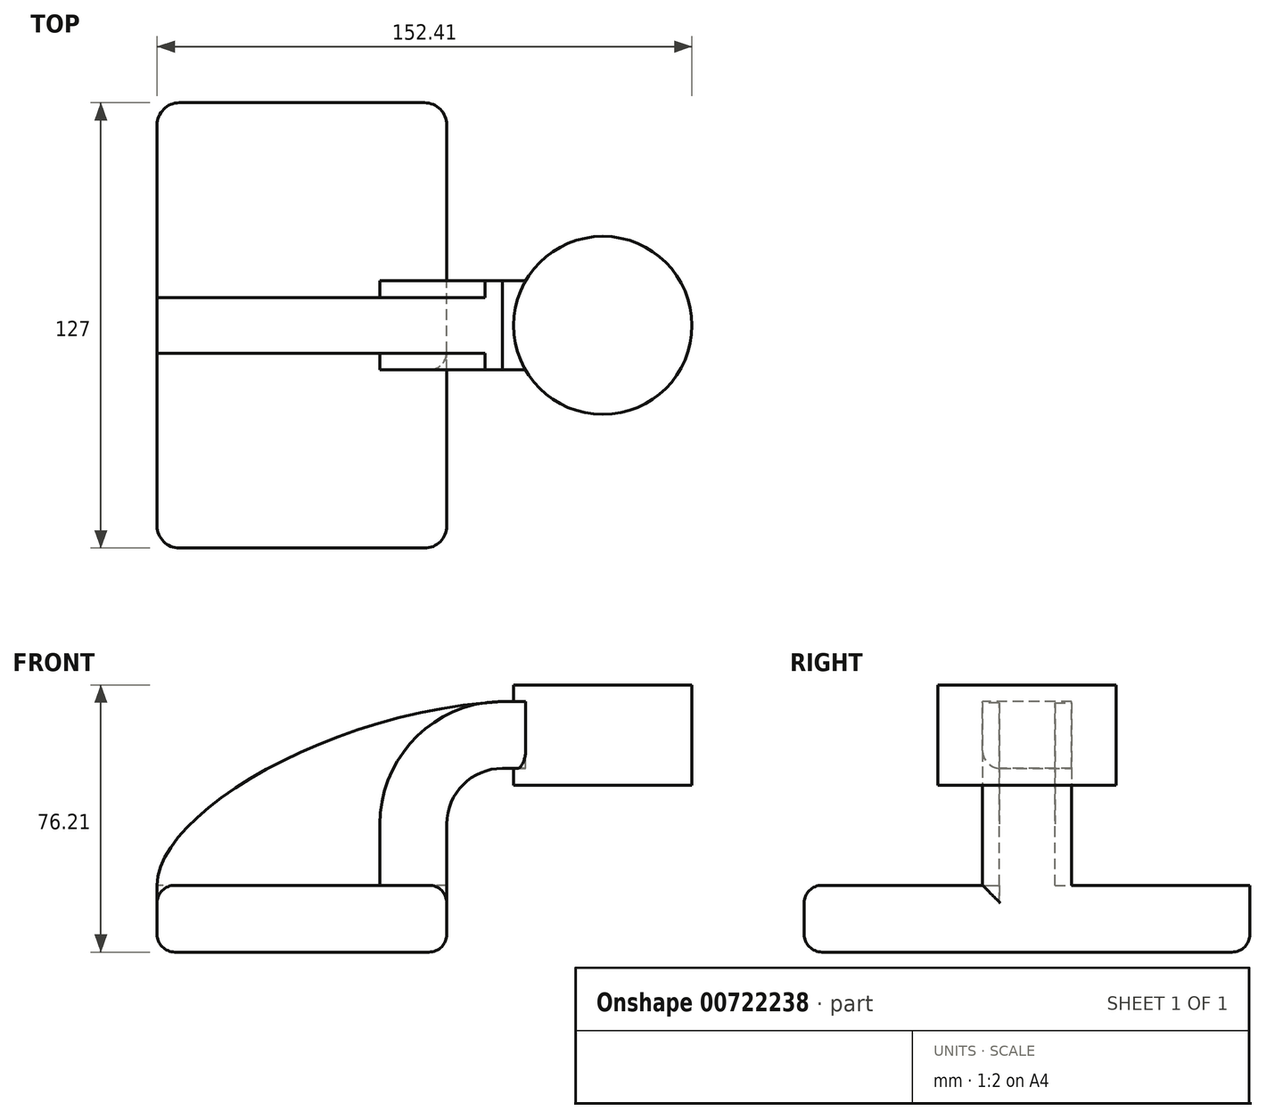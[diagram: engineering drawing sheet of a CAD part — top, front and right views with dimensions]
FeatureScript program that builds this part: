
annotation { "Feature Type Name" : "Feature", "Feature Type Description" : "" }
export const myFeature = defineFeature(function(context is Context, id is Id, definition is map)
    precondition{}
    {
        {
            var Q0;
            Q0=qCreatedBy(makeId("Front.planeOp"),FACE);
            var sketch = newSketch(context, id + "F0", { "sketchPlane" : qUnion([Q0])});
            skLineSegment(sketch, "E0.bottom", {"start": v(-41.28, -9.53) * mm, "end": v(41.28, -9.53) * mm});
            skLineSegment(sketch, "E0.top", {"start": v(-41.28, 9.52) * mm, "end": v(41.28, 9.52) * mm});
            skLineSegment(sketch, "E0.left", {"start": v(-41.28, -9.53) * mm, "end": v(-41.28, 9.52) * mm});
            skLineSegment(sketch, "E0.right", {"start": v(41.28, -9.53) * mm, "end": v(41.28, 9.52) * mm});
            skPoint(sketch, "E0.middle", {"position": v(0, 0) * mm});
            skLineSegment(sketch, "E1", {"start": v(41.28, 9.52) * mm, "end": v(41.28, 27) * mm});
            skArc(sketch, "E2", {"start": v(41.27, 27) * mm, "mid": v(45.92, 38.23) * mm, "end": v(57.15, 42.88) * mm});
            skLineSegment(sketch, "E3", {"start": v(57.15, 42.88) * mm, "end": v(85.72, 42.88) * mm});
            skLineSegment(sketch, "E4.bottom", {"start": v(111.12, 38.1) * mm, "end": v(60.33, 38.1) * mm});
            skLineSegment(sketch, "E4.top", {"start": v(111.12, 66.68) * mm, "end": v(60.33, 66.68) * mm});
            skLineSegment(sketch, "E4.left", {"start": v(111.12, 38.1) * mm, "end": v(111.12, 66.68) * mm});
            skLineSegment(sketch, "E4.right", {"start": v(60.33, 38.1) * mm, "end": v(60.33, 66.67) * mm});
            skPoint(sketch, "E4.middle", {"position": v(85.72, 52.39) * mm});
            skLineSegment(sketch, "E5.0", {"start": v(57.15, 61.93) * mm, "end": v(85.72, 61.93) * mm});
            skArc(sketch, "E5.1", {"start": v(22.23, 27) * mm, "mid": v(32.45, 51.7) * mm, "end": v(57.15, 61.93) * mm});
            skLineSegment(sketch, "E5.2", {"start": v(22.22, 9.52) * mm, "end": v(22.22, 27) * mm});
            skFitSpline(sketch, "E6", {"points": [v(-41.28, 9.52) * mm, v(57.15, 61.93) * mm], "startDerivative": vector(-0.56, 60.4) * mm, "endDerivative": vector(148.5, 7.89) * mm});
            skLineSegment(sketch, "E7", {"start": v(85.72, 66.68) * mm, "end": v(85.72, 38.1) * mm});
            skPoint(sketch, "E7.startSnap0", {"position": v(85.72, 66.68) * mm});
            skSolve(sketch);
        }
        {
            var Q0;
            Q0=makeQuery(id+"F0.imprint","IMPRINT",FACE,{"disambiguationData":[TD([[makeQuery(id+"F0.imprint","IMPRINT",EDGE,{"derivedFrom":sQuery(id+"F0.wireOp",EDGE,"E0.bottom")}),1.0]])]});
            extrude(context, id + "F1", {"entities" : qUnion([Q0]), "endBound" : BoundingType.SYMMETRIC, "depth" : 127 * mm, "offsetDistance" : 25.4 * mm});
        }
        {
            var Q0;
            {var subQ7=sQuery(id+"F0.wireOp",EDGE,"E1");Q0=makeQuery(id+"F0.imprint","IMPRINT",FACE,{"disambiguationData":[TD([[makeQuery(id+"F0.imprint","IMPRINT",EDGE,{"derivedFrom":subQ7}),1.0]])]});}
            var Q1;
            {var subQ0=sQuery(id+"F0.wireOp",EDGE,"E7");var subQ1=sQuery(id+"F0.wireOp",EDGE,"E3");var subQ2=makeQuery(id+"F0.imprint","INTERSECT",VERTEX,{"derivedFrom":[subQ1,subQ0]});Q1=makeQuery(id+"F0.imprint","IMPRINT",FACE,{"disambiguationData":[TD([[makeQuery(id+"F0.imprint","IMPRINT",EDGE,{"disambiguationData":[TD([[subQ2,1.0]])],"derivedFrom":subQ1}),1.0]])]});}
            extrude(context, id + "F2", {"entities" : qUnion([Q0, Q1]), "operationType" : NewBodyOperationType.ADD, "endBound" : BoundingType.SYMMETRIC, "depth" : 25.4 * mm, "offsetDistance" : 25.4 * mm});
        }
        {
            var Q0;
            {var subQ3=sQuery(id+"F0.wireOp",EDGE,"E5.2");Q0=makeQuery(id+"F0.imprint","IMPRINT",FACE,{"disambiguationData":[TD([[makeQuery(id+"F0.imprint","IMPRINT",EDGE,{"derivedFrom":subQ3}),1.0]])]});}
            extrude(context, id + "F3", {"entities" : qUnion([Q0]), "operationType" : NewBodyOperationType.ADD, "endBound" : BoundingType.SYMMETRIC, "depth" : 15.88 * mm, "offsetDistance" : 25.4 * mm});
        }
        {
            var Q0;
            {var subQ0=sQuery(id+"F0.wireOp",EDGE,"E4.left");Q0=makeQuery(id+"F0.imprint","IMPRINT",FACE,{"disambiguationData":[TD([[makeQuery(id+"F0.imprint","IMPRINT",EDGE,{"derivedFrom":subQ0}),1.0]])]});}
            var Q1;
            Q1=sQuery(id+"F0.wireOp",EDGE,"E7");
            revolve(context, id + "F4", {"operationType" : NewBodyOperationType.ADD, "surfaceOperationType" : NewSurfaceOperationType.NEW, "entities" : qUnion([Q0]), "axis" : qUnion([Q1]), "revolveType" : RevolveType.FULL});
        }
        {
            var Q0;
            Q0=makeQuery(id+"F1.opExtrude","CAP_EDGE",EDGE,{"disambiguationData":[OSD([sQuery(id+"F0.wireOp",EDGE,"E0.right")])],"isStart":false});
            var Q1;
            Q1=makeQuery(id+"F1.opExtrude","CAP_EDGE",EDGE,{"disambiguationData":[OSD([sQuery(id+"F0.wireOp",EDGE,"E0.left")])],"isStart":false});
            var Q2;
            Q2=makeQuery(id+"F1.opExtrude","CAP_EDGE",EDGE,{"disambiguationData":[OSD([sQuery(id+"F0.wireOp",EDGE,"E0.right")])],"isStart":true});
            var Q3;
            Q3=makeQuery(id+"F1.opExtrude","CAP_EDGE",EDGE,{"disambiguationData":[OSD([sQuery(id+"F0.wireOp",EDGE,"E0.left")])],"isStart":true});
            fillet(context, id + "F5", {"entities" : qUnion([Q0, Q1, Q2, Q3]), "radius" : 6.35 * mm, "tangentPropagation" : true, "allowEdgeOverflow" : false});
        }
        {
            var Q0;
            {var subQ4=sQuery(id+"F0.wireOp",EDGE,"E0.top");var subQ5=sQuery(id+"F0.wireOp",EDGE,"E0.right");var subQ6=sQuery(id+"F0.wireOp",EDGE,"E0.left");Q0=makeQuery(id+"F5.opFillet","BLEND_EDGE",EDGE,{"blendedFrom":[makeQuery(id+"F1.opExtrude","CAP_EDGE",EDGE,{"disambiguationData":[OSD([subQ5])],"isStart":false}),makeQuery(id+"F3.boolean.opBoolean","SPLIT",FACE,{"disambiguationData":[TD([makeQuery(id+"F1.opExtrude","CAP_FACE",FACE,{"disambiguationData":[OSD([sQuery(id+"F0.wireOp",EDGE,"E0.bottom"),subQ4,subQ6,subQ5])],"isStart":false})])],"derivedFrom":makeQuery(id+"F1.opExtrude","SWEPT_FACE",FACE,{"disambiguationData":[OSD([subQ4])]})})],"blendedInto":[makeQuery(id+"F3.boolean.opBoolean","SPLIT",FACE,{"disambiguationData":[TD([makeQuery(id+"F1.opExtrude","CAP_FACE",FACE,{"disambiguationData":[OSD([sQuery(id+"F0.wireOp",EDGE,"E0.bottom"),subQ4,subQ6,subQ5])],"isStart":false})])],"derivedFrom":makeQuery(id+"F1.opExtrude","SWEPT_FACE",FACE,{"disambiguationData":[OSD([subQ4])]})})]});}
            var Q1;
            Q1=makeQuery(id+"F1.opExtrude","SWEPT_EDGE",EDGE,{"disambiguationData":[OSD([sQuery(id+"F0.wireOp",EDGE,"E0.bottom"),sQuery(id+"F0.wireOp",EDGE,"E0.right")])]});
            var Q2;
            Q2=makeQuery(id+"F2.opExtrude","CAP_EDGE",EDGE,{"disambiguationData":[OSD([sQuery(id+"F0.wireOp",EDGE,"E1")])],"isStart":false});
            fillet(context, id + "F6", {"entities" : qUnion([Q0, Q1, Q2]), "radius" : 5.08 * mm, "tangentPropagation" : true, "allowEdgeOverflow" : false});
        }
    });
